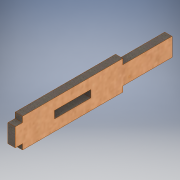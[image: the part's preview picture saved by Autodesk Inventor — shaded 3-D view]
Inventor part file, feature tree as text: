
AUTODESK INVENTOR PART (.ipt)
format: ipt  version: 2019 (Build 230136000, 136)  size: 133,632 bytes
history: native  units: mm
features: extrude x1, sketch x1
ambient origin geometry x8: Origin, YZ Plane, XZ Plane, XY Plane, X Axis, Y Axis, Z Axis, Center Point
bodies: Body1 (feature_tree)
feature tree (2):
  extrude  "Выдавливание2"  Depth=10.0mm
  sketch  "Эскиз1"
